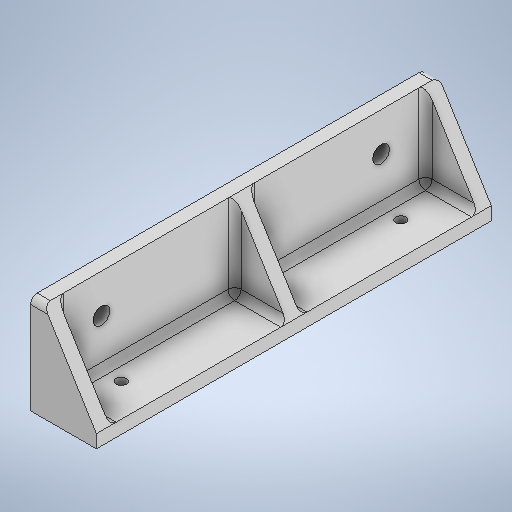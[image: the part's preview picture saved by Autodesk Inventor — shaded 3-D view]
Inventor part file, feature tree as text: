
AUTODESK INVENTOR PART (.ipt)
format: ipt  version: 2025 (Build 290162000, 162)  size: 331,264 bytes
history: native  units: in
note: dims shown in document units (in); Inventor stores cm internally (conversion verified against a paired STEP export)
features: sketch x5, extrude x3, fillet x2, hole x2, mirror x2, pattern_linear x1, plane x1
ambient origin geometry x8: Origin, YZ Plane, XZ Plane, XY Plane, X Axis, Y Axis, Z Axis, Center Point
bodies: Solid1 (feature_tree)
feature tree (16):
  extrude  "Extrusion1"  Depth=0.7874in
  extrude  "Extrusion2"  Depth=0.1575in
  pattern_linear  "Rectangular Pattern1"  Count1=12 Spacing1=0.0in
  fillet  "Fillet1"  Radius=0.1575in
  hole  "Hole1"  [1 undecoded]
  mirror  "Mirror1"
  hole  "Hole2"  [1 undecoded]
  mirror  "Mirror2"
  plane  "Work Plane1"
  extrude  "Extrusion3"  Depth=0.3937in
  fillet  "Fillet2"  Radius=1.6732in
  sketch  "Sketch1"  dims[d0=1.1811in d1=0.7874in]
  sketch  "Sketch2"  dims[d2=0.1575in d3=0.1575in d4=4.7244in d5=0.0in d6=0.1575in d7=0.0in]
  sketch  "Sketch3"  dims[d8=1.1811in d10=2.2835in d11=0.0787in]
  sketch  "Sketch4"  dims[d12=0.2008in d13=0.2362in d14=0.1575in d15=0.0787in d16=90.0deg d17=0.315in d18=0.8108in d19=0.7197in]
  sketch  "Sketch5"  dims[d20=1.6732in d21=0.122in d22=0.2362in d23=0.1575in d24=0.0787in d25=90.0deg d26=0.315in d27=0.8108in d28=0.3937in d29=1.6732in d30=-0.7197in d31=0.1378in d32=1.2205in d33=0.1378in d34=0.4724in d35=0.1181in d36=0.0in d37=0.0394in]
note: 2 required parameter values undecoded (feature->parameter linkage not recoverable at this tier; creation-order binding heuristic only, values carry confidence <= 0.55)
